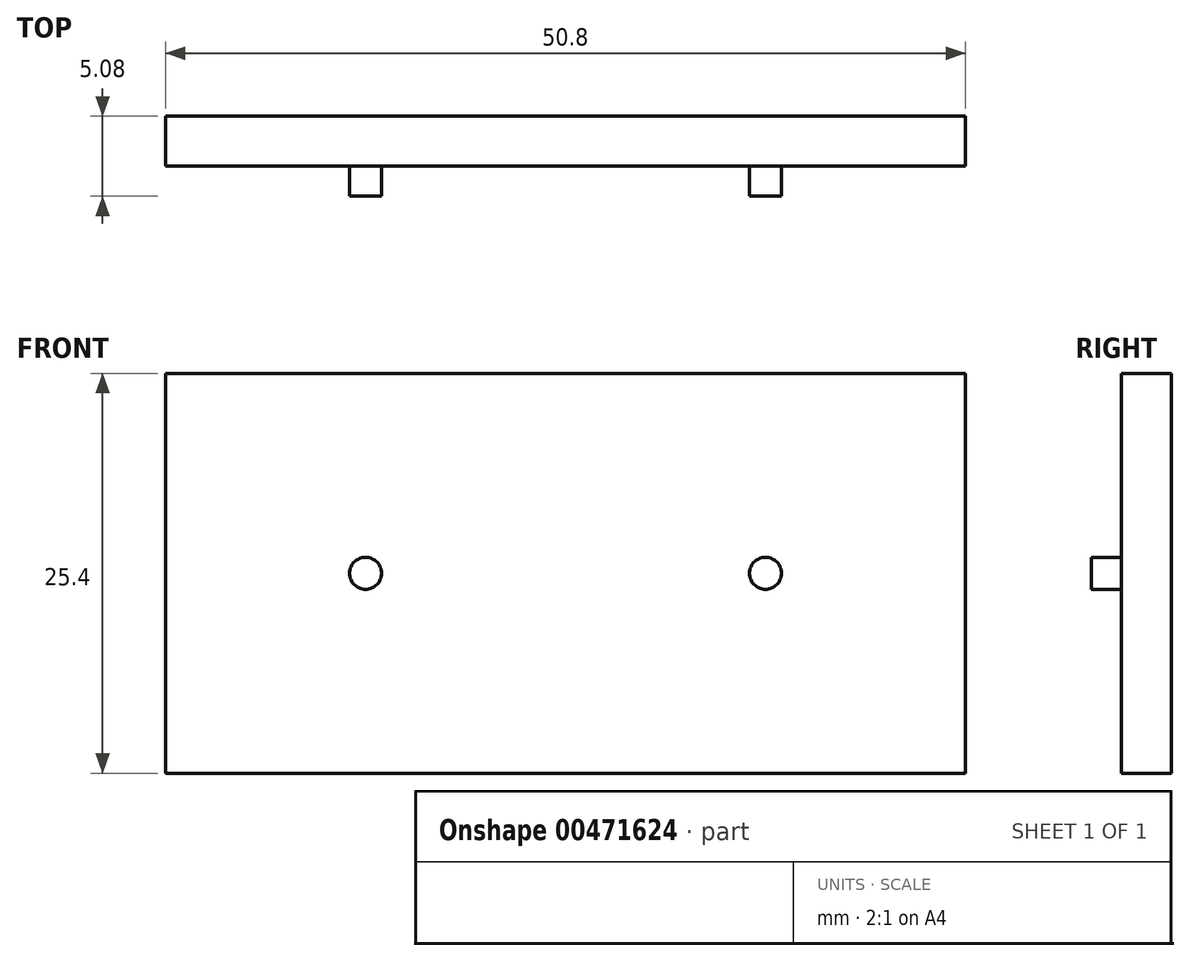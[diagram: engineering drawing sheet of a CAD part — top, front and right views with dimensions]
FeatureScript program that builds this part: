
annotation { "Feature Type Name" : "Feature", "Feature Type Description" : "" }
export const myFeature = defineFeature(function(context is Context, id is Id, definition is map)
    precondition{}
    {
        {
            var Q0;
            Q0=qCreatedBy(makeId("Front.planeOp"),FACE);
            var sketch = newSketch(context, id + "F0", { "sketchPlane" : qUnion([Q0])});
            skLineSegment(sketch, "E0.bottom", {"start": v(-25.4, 25.4) * mm, "end": v(25.4, 25.4) * mm});
            skLineSegment(sketch, "E0.top", {"start": v(-25.4, 0) * mm, "end": v(25.4, 0) * mm});
            skLineSegment(sketch, "E0.left", {"start": v(-25.4, 25.4) * mm, "end": v(-25.4, 0) * mm});
            skLineSegment(sketch, "E0.right", {"start": v(25.4, 25.4) * mm, "end": v(25.4, 0) * mm});
            skCircle(sketch, "E1", {"center": v(-12.7, 12.7) * mm, "radius": 1.02 * mm});
            skCircle(sketch, "E2", {"center": v(12.7, 12.7) * mm, "radius": 1.02 * mm});
            skLineSegment(sketch, "E3", {"start": v(0, 169.8) * mm, "end": v(0, -119.41) * mm, "construction": true});
            skLineSegment(sketch, "E4", {"start": v(-140.4, 0) * mm, "end": v(175.4, 0) * mm, "construction": true});
            skSolve(sketch);
        }
        {
            var Q0;
            Q0=makeQuery(id+"F0.imprint","IMPRINT",FACE,{"disambiguationData":[TD([[makeQuery(id+"F0.imprint","IMPRINT",EDGE,{"derivedFrom":sQuery(id+"F0.wireOp",EDGE,"E1")}),1.0]])]});
            var Q1;
            Q1=makeQuery(id+"F0.imprint","IMPRINT",FACE,{"disambiguationData":[TD([[makeQuery(id+"F0.imprint","IMPRINT",EDGE,{"derivedFrom":sQuery(id+"F0.wireOp",EDGE,"E0.bottom")}),-1.0]])]});
            var Q2;
            Q2=makeQuery(id+"F0.imprint","IMPRINT",FACE,{"disambiguationData":[TD([[makeQuery(id+"F0.imprint","IMPRINT",EDGE,{"derivedFrom":sQuery(id+"F0.wireOp",EDGE,"E2")}),1.0]])]});
            extrude(context, id + "F1", {"entities" : qUnion([Q0, Q1, Q2]), "depth" : 3.17 * mm});
        }
        {
            var Q0;
            Q0=makeQuery(id+"F0.imprint","IMPRINT",FACE,{"disambiguationData":[TD([[makeQuery(id+"F0.imprint","IMPRINT",EDGE,{"derivedFrom":sQuery(id+"F0.wireOp",EDGE,"E2")}),1.0]])]});
            var Q1;
            Q1=makeQuery(id+"F0.imprint","IMPRINT",FACE,{"disambiguationData":[TD([[makeQuery(id+"F0.imprint","IMPRINT",EDGE,{"derivedFrom":sQuery(id+"F0.wireOp",EDGE,"E1")}),1.0]])]});
            extrude(context, id + "F2", {"entities" : qUnion([Q0, Q1]), "operationType" : NewBodyOperationType.ADD, "depth" : 5.08 * mm});
        }
    });
